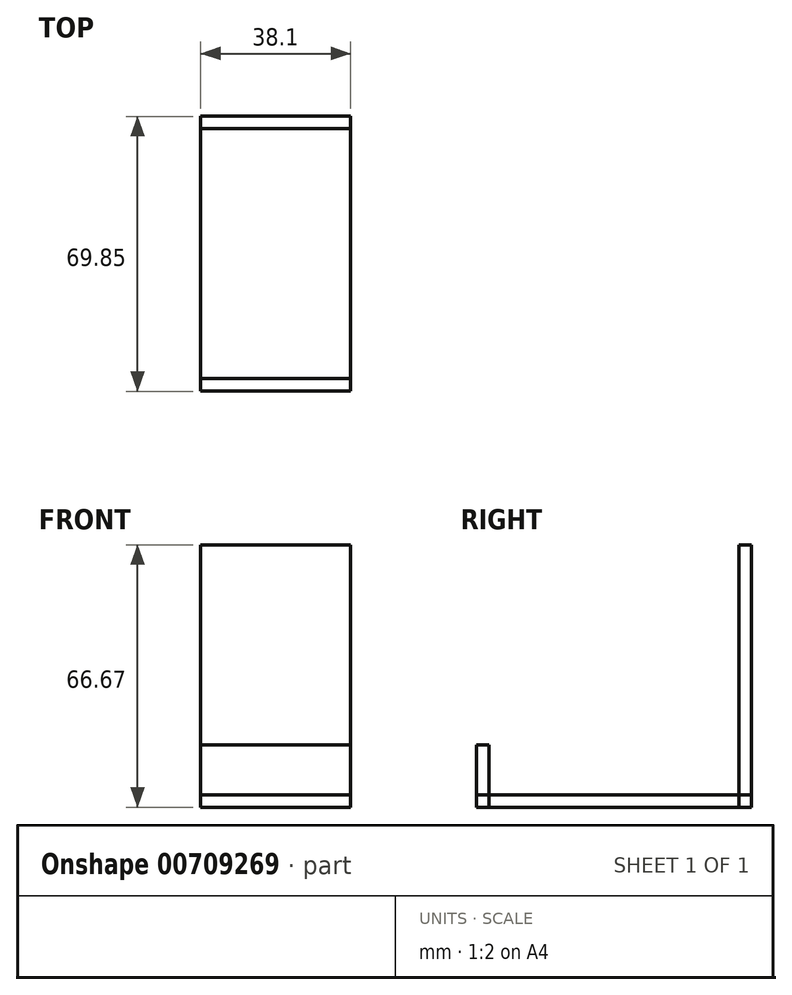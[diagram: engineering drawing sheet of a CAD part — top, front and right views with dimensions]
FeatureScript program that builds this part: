
annotation { "Feature Type Name" : "Feature", "Feature Type Description" : "" }
export const myFeature = defineFeature(function(context is Context, id is Id, definition is map)
    precondition{}
    {
        {
            var Q0;
            Q0=qCreatedBy(makeId("Top.planeOp"),FACE);
            var sketch = newSketch(context, id + "F0", { "sketchPlane" : qUnion([Q0])});
            skLineSegment(sketch, "E0.bottom", {"start": v(-24.74, 44.14) * mm, "end": v(13.36, 44.14) * mm});
            skLineSegment(sketch, "E0.top", {"start": v(-24.74, -19.36) * mm, "end": v(13.36, -19.36) * mm});
            skLineSegment(sketch, "E0.left", {"start": v(-24.74, 44.14) * mm, "end": v(-24.74, -19.36) * mm});
            skLineSegment(sketch, "E0.right", {"start": v(13.36, 44.14) * mm, "end": v(13.36, -19.36) * mm});
            skSolve(sketch);
        }
        {
            var Q0;
            Q0=makeQuery(id+"F0.imprint","IMPRINT",FACE,{"disambiguationData":[TD([[makeQuery(id+"F0.imprint","IMPRINT",EDGE,{"derivedFrom":sQuery(id+"F0.wireOp",EDGE,"E0.bottom")}),-1.0]])]});
            extrude(context, id + "F1", {"entities" : qUnion([Q0]), "depth" : 3.17 * mm, "offsetDistance" : 25.4 * mm});
        }
        {
            var Q0;
            Q0=makeQuery(id+"F1.opExtrude","CAP_FACE",FACE,{"disambiguationData":[OSD([sQuery(id+"F0.wireOp",EDGE,"E0.bottom"),sQuery(id+"F0.wireOp",EDGE,"E0.top"),sQuery(id+"F0.wireOp",EDGE,"E0.left"),sQuery(id+"F0.wireOp",EDGE,"E0.right")])],"isStart":false});
            var sketch = newSketch(context, id + "F2", { "sketchPlane" : qUnion([Q0])});
            skLineSegment(sketch, "E1.bottom", {"start": v(-24.74, 44.14) * mm, "end": v(13.36, 44.14) * mm});
            skLineSegment(sketch, "E1.top", {"start": v(-24.74, 47.31) * mm, "end": v(13.36, 47.31) * mm});
            skLineSegment(sketch, "E1.left", {"start": v(-24.74, 44.14) * mm, "end": v(-24.74, 47.31) * mm});
            skLineSegment(sketch, "E1.right", {"start": v(13.36, 44.14) * mm, "end": v(13.36, 47.31) * mm});
            skSolve(sketch);
        }
        {
            var Q0;
            Q0=makeQuery(id+"F2.imprint","IMPRINT",FACE,{"disambiguationData":[TD([[makeQuery(id+"F2.imprint","IMPRINT",EDGE,{"derivedFrom":sQuery(id+"F2.wireOp",EDGE,"E1.bottom")}),1.0]])]});
            extrude(context, id + "F3", {"entities" : qUnion([Q0]), "depth" : 63.5 * mm, "offsetDistance" : 25.4 * mm});
        }
        {
            var Q0;
            Q0=makeQuery(id+"F1.opExtrude","SWEPT_FACE",FACE,{"disambiguationData":[OSD([sQuery(id+"F0.wireOp",EDGE,"E0.bottom")])]});
            extrude(context, id + "F4", {"entities" : qUnion([Q0]), "depth" : 3.17 * mm, "offsetDistance" : 25.4 * mm});
        }
        {
            var Q0;
            Q0=makeQuery(id+"F1.opExtrude","CAP_FACE",FACE,{"disambiguationData":[OSD([sQuery(id+"F0.wireOp",EDGE,"E0.bottom"),sQuery(id+"F0.wireOp",EDGE,"E0.top"),sQuery(id+"F0.wireOp",EDGE,"E0.left"),sQuery(id+"F0.wireOp",EDGE,"E0.right")])],"isStart":false});
            var sketch = newSketch(context, id + "F5", { "sketchPlane" : qUnion([Q0])});
            skLineSegment(sketch, "E2.bottom", {"start": v(13.36, -19.36) * mm, "end": v(-24.74, -19.36) * mm});
            skLineSegment(sketch, "E2.top", {"start": v(13.36, -22.54) * mm, "end": v(-24.74, -22.54) * mm});
            skLineSegment(sketch, "E2.left", {"start": v(13.36, -19.36) * mm, "end": v(13.36, -22.54) * mm});
            skLineSegment(sketch, "E2.right", {"start": v(-24.74, -19.36) * mm, "end": v(-24.74, -22.54) * mm});
            skSolve(sketch);
        }
        {
            var Q0;
            Q0=makeQuery(id+"F5.imprint","IMPRINT",FACE,{"disambiguationData":[TD([[makeQuery(id+"F5.imprint","IMPRINT",EDGE,{"derivedFrom":sQuery(id+"F5.wireOp",EDGE,"E2.bottom")}),-1.0]])]});
            extrude(context, id + "F6", {"entities" : qUnion([Q0]), "depth" : 12.7 * mm, "offsetDistance" : 25.4 * mm});
        }
        {
            var Q0;
            Q0=makeQuery(id+"F1.opExtrude","SWEPT_FACE",FACE,{"disambiguationData":[OSD([sQuery(id+"F0.wireOp",EDGE,"E0.top")])]});
            extrude(context, id + "F7", {"entities" : qUnion([Q0]), "depth" : 3.17 * mm, "offsetDistance" : 25.4 * mm});
        }
    });
